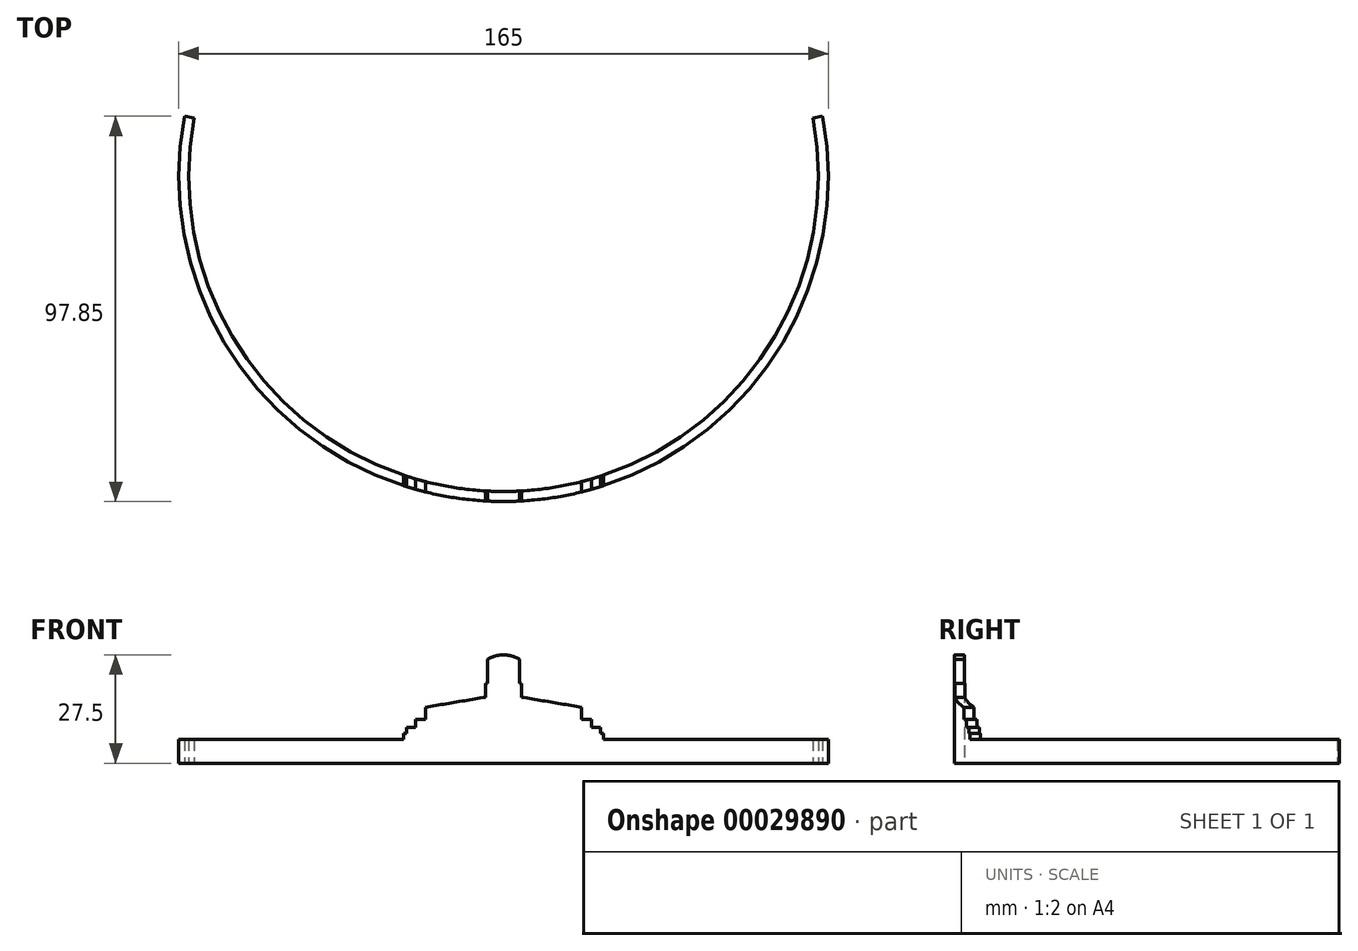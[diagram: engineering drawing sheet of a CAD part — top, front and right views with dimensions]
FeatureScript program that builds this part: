
annotation { "Feature Type Name" : "Feature", "Feature Type Description" : "" }
export const myFeature = defineFeature(function(context is Context, id is Id, definition is map)
    precondition{}
    {
        {
            var Q0;
            Q0=qCreatedBy(makeId("Front.planeOp"),FACE);
            var sketch = newSketch(context, id + "F0", { "sketchPlane" : qUnion([Q0])});
            skLineSegment(sketch, "E0", {"start": v(-67.31, 0) * mm, "end": v(67.31, 0) * mm});
            skLineSegment(sketch, "E1", {"start": v(67.31, 0) * mm, "end": v(67.31, 15.24) * mm});
            skLineSegment(sketch, "E2", {"start": v(67.31, 15.24) * mm, "end": v(63.5, 15.24) * mm});
            skLineSegment(sketch, "E3", {"start": v(63.5, 15.24) * mm, "end": v(63.5, 19.05) * mm});
            skLineSegment(sketch, "E4", {"start": v(63.5, 19.05) * mm, "end": v(61.6, 19.05) * mm});
            skLineSegment(sketch, "E5", {"start": v(61.6, 19.05) * mm, "end": v(61.6, 22.86) * mm});
            skLineSegment(sketch, "E6", {"start": v(61.6, 22.86) * mm, "end": v(55.88, 22.86) * mm});
            skLineSegment(sketch, "E7", {"start": v(55.88, 22.86) * mm, "end": v(55.88, 27.94) * mm});
            skLineSegment(sketch, "E8", {"start": v(55.88, 27.94) * mm, "end": v(49.53, 27.94) * mm});
            skLineSegment(sketch, "E9", {"start": v(49.53, 27.94) * mm, "end": v(49.53, 35.56) * mm});
            skLineSegment(sketch, "E10", {"start": v(49.53, 35.56) * mm, "end": v(11.43, 41.91) * mm});
            skLineSegment(sketch, "E11", {"start": v(11.43, 41.91) * mm, "end": v(11.43, 50.8) * mm});
            skLineSegment(sketch, "E12", {"start": v(11.43, 50.8) * mm, "end": v(10.16, 50.8) * mm});
            skLineSegment(sketch, "E13", {"start": v(10.16, 50.8) * mm, "end": v(10.16, 66.04) * mm});
            skLineSegment(sketch, "E14", {"start": v(10.16, 66.04) * mm, "end": v(0, 66.04) * mm, "construction": true});
            skLineSegment(sketch, "E15", {"start": v(0, 66.04) * mm, "end": v(0, 0) * mm, "construction": true});
            skLineSegment(sketch, "E16.MirrorCS", {"start": v(-10.16, 66.04) * mm, "end": v(0, 66.04) * mm, "construction": true});
            skLineSegment(sketch, "E17.MirrorCS", {"start": v(-10.16, 50.8) * mm, "end": v(-10.16, 66.04) * mm});
            skLineSegment(sketch, "E18.MirrorCS", {"start": v(-11.43, 41.91) * mm, "end": v(-11.43, 50.8) * mm});
            skLineSegment(sketch, "E19.MirrorCS", {"start": v(-49.53, 35.56) * mm, "end": v(-11.43, 41.91) * mm});
            skLineSegment(sketch, "E20.MirrorCS", {"start": v(-49.53, 27.94) * mm, "end": v(-49.53, 35.56) * mm});
            skLineSegment(sketch, "E21.MirrorCS", {"start": v(-55.88, 27.94) * mm, "end": v(-49.53, 27.94) * mm});
            skLineSegment(sketch, "E22.MirrorCS", {"start": v(-55.88, 22.86) * mm, "end": v(-55.88, 27.94) * mm});
            skLineSegment(sketch, "E23.MirrorCS", {"start": v(-61.6, 22.86) * mm, "end": v(-55.88, 22.86) * mm});
            skLineSegment(sketch, "E24.MirrorCS", {"start": v(-61.6, 19.05) * mm, "end": v(-61.6, 22.86) * mm});
            skLineSegment(sketch, "E25.MirrorCS", {"start": v(-63.5, 15.24) * mm, "end": v(-63.5, 19.05) * mm});
            skLineSegment(sketch, "E26.MirrorCS", {"start": v(-67.31, 15.24) * mm, "end": v(-63.5, 15.24) * mm});
            skLineSegment(sketch, "E27.MirrorCS", {"start": v(-67.31, 0) * mm, "end": v(-67.31, 15.24) * mm});
            skLineSegment(sketch, "E28", {"start": v(-63.5, 19.05) * mm, "end": v(-61.6, 19.05) * mm});
            skLineSegment(sketch, "E29", {"start": v(-10.16, 50.8) * mm, "end": v(-11.43, 50.8) * mm});
            skArc(sketch, "E30", {"start": v(10.16, 66.04) * mm, "mid": v(0, 68.76) * mm, "end": v(-10.16, 66.04) * mm});
            skSolve(sketch);
        }
        {
            var Q0;
            Q0=qCreatedBy(makeId("Top.planeOp"),FACE);
            var sketch = newSketch(context, id + "F1", { "sketchPlane" : qUnion([Q0])});
            skArc(sketch, "E31", {"start": v(-81.06, 97.85) * mm, "mid": v(0, 0) * mm, "end": v(81.06, 97.85) * mm});
            skArc(sketch, "E32.0", {"start": v(-78.56, 97.38) * mm, "mid": v(0, 2.54) * mm, "end": v(78.56, 97.38) * mm});
            skLineSegment(sketch, "E33", {"start": v(-78.56, 97.38) * mm, "end": v(-81.06, 97.85) * mm});
            skLineSegment(sketch, "E34", {"start": v(81.06, 97.85) * mm, "end": v(78.56, 97.38) * mm});
            skSolve(sketch);
        }
        {
            var Q0;
            Q0=qSketchRegion(id+"F0",true);
            extrude(context, id + "F2", {"entities" : qUnion([Q0]), "oppositeDirection" : true, "depth" : 48.53 * mm});
        }
        {
            var Q0;
            Q0=makeQuery(id+"F2.opExtrude","SWEPT_BODY",BODY,{"disambiguationData":[OSD([sQuery(id+"F0.wireOp",EDGE,"E0"),sQuery(id+"F0.wireOp",EDGE,"E1"),sQuery(id+"F0.wireOp",EDGE,"E2"),sQuery(id+"F0.wireOp",EDGE,"E3"),sQuery(id+"F0.wireOp",EDGE,"E4"),sQuery(id+"F0.wireOp",EDGE,"E5"),sQuery(id+"F0.wireOp",EDGE,"E6"),sQuery(id+"F0.wireOp",EDGE,"E7"),sQuery(id+"F0.wireOp",EDGE,"E8"),sQuery(id+"F0.wireOp",EDGE,"E9"),sQuery(id+"F0.wireOp",EDGE,"E10"),sQuery(id+"F0.wireOp",EDGE,"E11"),sQuery(id+"F0.wireOp",EDGE,"E12"),sQuery(id+"F0.wireOp",EDGE,"E13"),sQuery(id+"F0.wireOp",EDGE,"E17.MirrorCS"),sQuery(id+"F0.wireOp",EDGE,"E18.MirrorCS"),sQuery(id+"F0.wireOp",EDGE,"E19.MirrorCS"),sQuery(id+"F0.wireOp",EDGE,"E20.MirrorCS"),sQuery(id+"F0.wireOp",EDGE,"E21.MirrorCS"),sQuery(id+"F0.wireOp",EDGE,"E22.MirrorCS"),sQuery(id+"F0.wireOp",EDGE,"E23.MirrorCS"),sQuery(id+"F0.wireOp",EDGE,"E24.MirrorCS"),sQuery(id+"F0.wireOp",EDGE,"E25.MirrorCS"),sQuery(id+"F0.wireOp",EDGE,"E26.MirrorCS"),sQuery(id+"F0.wireOp",EDGE,"E27.MirrorCS"),sQuery(id+"F0.wireOp",EDGE,"E28"),sQuery(id+"F0.wireOp",EDGE,"E29"),sQuery(id+"F0.wireOp",EDGE,"E30")])]});
            var Q1;
            Q1=qCreatedBy(makeId("Origin.pointOp"),VERTEX);
            transform(context, id + "F3", {"entities" : qUnion([Q0]), "transformType" : TransformType.SCALE_UNIFORMLY, "scale" : .4, "makeCopy" : false, "scalePoint" : qUnion([Q1])});
        }
        {
            var Q0;
            Q0=qSketchRegion(id+"F1",true);
            extrude(context, id + "F4", {"entities" : qUnion([Q0]), "operationType" : NewBodyOperationType.INTERSECT, "depth" : 76.2 * mm});
        }
        {
            var Q0;
            Q0 = qSketchRegion(id + "F1", true);
            var Q1;
            Q1=makeQuery(id+"F2.opExtrude","SWEPT_FACE",FACE,{"disambiguationData":[OSD([sQuery(id+"F0.wireOp",EDGE,"E26.MirrorCS")])]});
            extrude(context, id + "F5", {"entities" : qUnion([Q0]), "operationType" : NewBodyOperationType.ADD, "endBound" : BoundingType.UP_TO_SURFACE, "endBoundEntityFace" : qUnion([Q1]), "depth" : 3.1 * mm});
        }
    });
